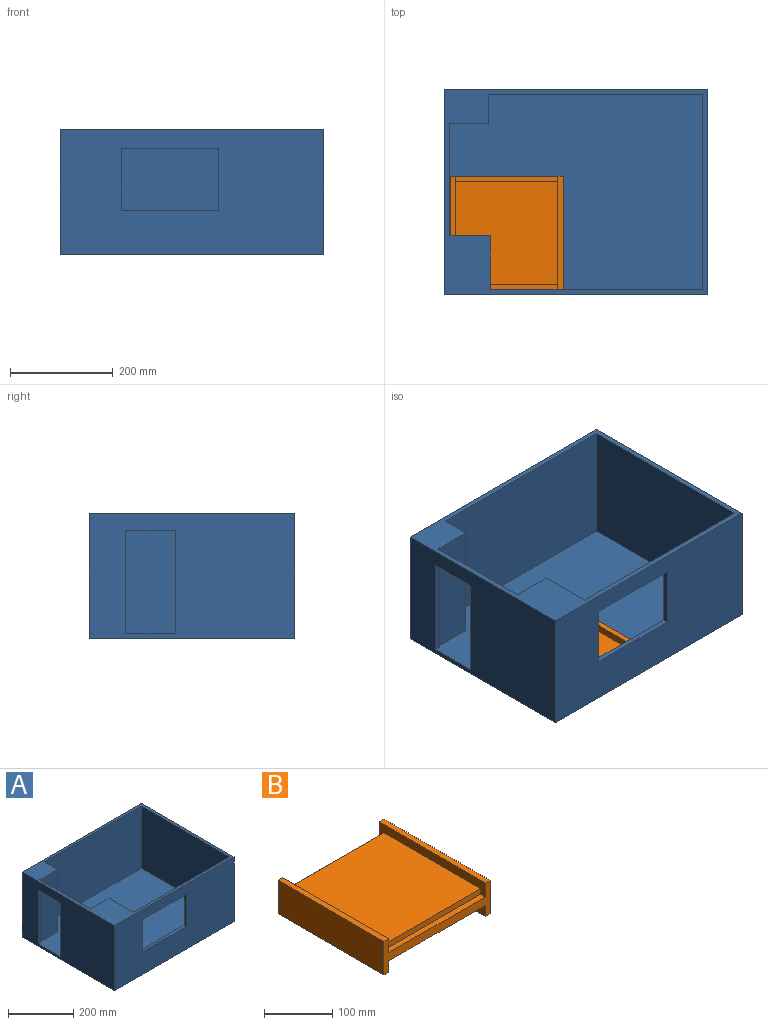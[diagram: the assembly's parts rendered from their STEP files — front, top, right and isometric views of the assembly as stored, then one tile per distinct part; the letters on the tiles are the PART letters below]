
ASSEMBLY  parts=2 mates=1
PART A: 22 faces, bbox 515x401x243 mm
  f0: plane 495x233mm, normal (0,1,0), area 89695mm2, adj f6,f7,f11,f12,f16,f17,f18,f19
  f1: plane 401x243mm, normal (-1,0,0), area 77946mm2, adj f2,f4,f5,f6,f12,f13,f14,f15
  f2: plane 515x243mm, normal (0,-1,0), area 102345mm2, adj f1,f3,f5,f12,f16,f17,f18,f19
  f3: plane 401x243mm, normal (1,0,0), area 97443mm2, adj f2,f4,f5,f12
  f4: plane 515x243mm, normal (0,1,0), area 125145mm2, adj f1,f3,f5,f12
  f5: plane 515x401mm, normal (0,0,-1), area 206515mm2, adj f1,f2,f3,f4
  f6: plane 505x381mm, normal (0,0,1), area 185176mm2, adj f0,f1,f7,f8,f9,f10,f11,f13
  f7: plane 324x233mm, normal (1,0,0), area 48540mm2, adj f0,f6,f8,f12,f13,f14,f15,f20
  f8: plane 233x77mm, normal (0,-1,0), area 17941mm2, adj f6,f7,f9,f12
  f9: plane 233x57mm, normal (1,0,0), area 13281mm2, adj f6,f8,f10,f12
  f10: plane 418x233mm, normal (0,-1,0), area 97394mm2, adj f6,f9,f11,f12
  f11: plane 381x233mm, normal (-1,0,0), area 88773mm2, adj f0,f6,f10,f12
  f12: plane 515x401mm, normal (0,0,1), area 30709mm2, adj f0,f1,f2,f3,f4,f7,f8,f9
  f13: plane 201x10mm, normal (0,-1,0), area 2010mm2, adj f1,f6,f7,f15
  f14: plane 201x10mm, normal (0,1,0), area 2010mm2, adj f1,f6,f7,f15
  f15: plane 97x10mm, normal (0,0,-1), area 970mm2, adj f1,f7,f13,f14
  f16: plane 120x10mm, normal (1,0,0), area 1200mm2, adj f0,f2,f18,f19
  f17: plane 120x10mm, normal (-1,0,0), area 1200mm2, adj f0,f2,f18,f19
  f18: plane 190x10mm, normal (0,0,-1), area 1900mm2, adj f0,f2,f16,f17
  f19: plane 190x10mm, normal (0,0,1), area 1900mm2, adj f0,f2,f16,f17
  f20: plane 105x80mm, normal (0.66,0,-0.75), area 11231.1mm2, adj f0,f7,f12,f21
  f21: plane 80x71mm, normal (0,1,0), area 2840mm2, adj f7,f12,f20
PART B: 18 faces, bbox 220x220x60 mm
  f0: plane 220x10mm, normal (0,0,-1), area 2200mm2, adj f4,f5,f6,f7
  f1: plane 220x25mm, normal (-1,0,0), area 3500mm2, adj f4,f6,f8,f12,f13,f15,f16,f17
  f2: plane 220x25mm, normal (1,0,0), area 3500mm2, adj f4,f6,f11,f12,f13,f15,f16,f17
  f3: plane 220x10mm, normal (0,0,-1), area 2200mm2, adj f4,f6,f9,f10
  f4: plane 220x60mm, normal (0,1,0), area 4200mm2, adj f0,f1,f2,f3,f5,f7,f8,f9
  f5: plane 220x20mm, normal (-1,0,0), area 4400mm2, adj f0,f4,f6,f14
  f6: plane 220x60mm, normal (0,-1,0), area 4200mm2, adj f0,f1,f2,f3,f5,f7,f8,f9
  f7: plane 220x60mm, normal (1,0,0), area 13200mm2, adj f0,f4,f6,f8
  f8: plane 220x10mm, normal (0,0,1), area 2200mm2, adj f1,f4,f6,f7
  f9: plane 220x20mm, normal (1,0,0), area 4400mm2, adj f3,f4,f6,f14
  f10: plane 220x60mm, normal (-1,0,0), area 13200mm2, adj f3,f4,f6,f11
  f11: plane 220x10mm, normal (0,0,1), area 2200mm2, adj f2,f4,f6,f10
  f12: plane 200x10mm, normal (0,0,1), area 2000mm2, adj f1,f2,f6,f17
  f13: plane 200x10mm, normal (0,0,1), area 2000mm2, adj f1,f2,f4,f16
  f14: plane 220x200mm, normal (0,0,-1), area 44000mm2, adj f4,f5,f6,f9
  f15: plane 200x200mm, normal (0,0,1), area 40000mm2, adj f1,f2,f16,f17
  f16: plane 200x10mm, normal (0,1,0), area 2000mm2, adj f1,f2,f13,f15
  f17: plane 200x10mm, normal (0,-1,0), area 2000mm2, adj f1,f2,f12,f15
PLACE A t=(-251.13,-187.08,0)mm
PLACE B t=(-248.81,-186.1,0)mm
MATE planar B.f3 <-> A.f6  axis (0,0,-1) through (-243.81,-76.1,0)mm
